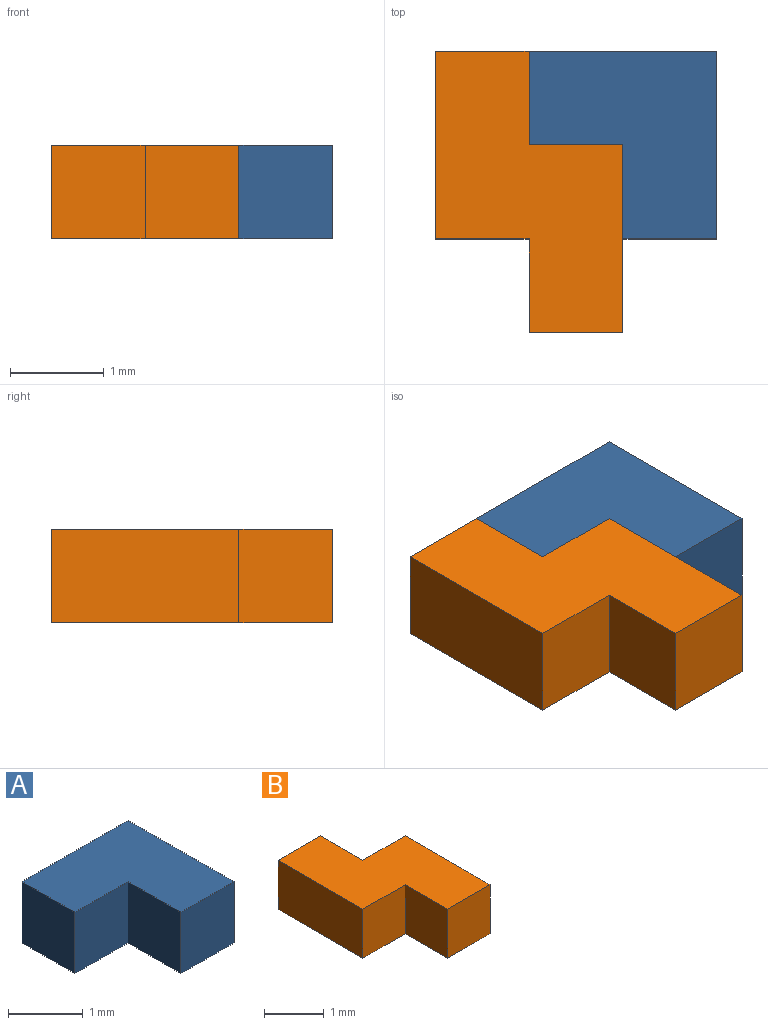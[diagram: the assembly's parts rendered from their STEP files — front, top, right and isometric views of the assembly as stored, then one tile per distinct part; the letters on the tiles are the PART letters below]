
ASSEMBLY  parts=2 mates=1
PART A: 8 faces, bbox 2x2x1 mm
  f0: plane 1x1mm, normal (-1,0,0), area 1mm2, adj f1,f3,f4,f5
  f1: plane 2x2mm, normal (0,0,-1), area 3mm2, adj f0,f2,f4,f5,f6,f7
  f2: plane 2x1mm, normal (1,0,0), area 2mm2, adj f1,f3,f5,f7
  f3: plane 2x2mm, normal (0,0,1), area 3mm2, adj f0,f2,f4,f5,f6,f7
  f4: plane 1x1mm, normal (0,-1,0), area 1mm2, adj f0,f1,f3,f6
  f5: plane 2x1mm, normal (0,1,0), area 2mm2, adj f0,f1,f2,f3
  f6: plane 1x1mm, normal (-1,0,0), area 1mm2, adj f1,f3,f4,f7
  f7: plane 1x1mm, normal (0,-1,0), area 1mm2, adj f1,f2,f3,f6
PART B: 10 faces, bbox 2x3x1 mm
  f0: plane 3x2mm, normal (0,0,-1), area 4mm2, adj f1,f3,f4,f5,f6,f7,f8,f9
  f1: plane 1x1mm, normal (1,0,0), area 1mm2, adj f0,f2,f5,f6
  f2: plane 3x2mm, normal (0,0,1), area 4mm2, adj f1,f3,f4,f5,f6,f7,f8,f9
  f3: plane 2x1mm, normal (-1,0,0), area 2mm2, adj f0,f2,f4,f5
  f4: plane 1x1mm, normal (0,-1,0), area 1mm2, adj f0,f2,f3,f8
  f5: plane 1x1mm, normal (0,1,0), area 1mm2, adj f0,f1,f2,f3
  f6: plane 1x1mm, normal (0,1,0), area 1mm2, adj f0,f1,f2,f7
  f7: plane 2x1mm, normal (1,0,0), area 2mm2, adj f0,f2,f6,f9
  f8: plane 1x1mm, normal (-1,0,0), area 1mm2, adj f0,f2,f4,f9
  f9: plane 1x1mm, normal (0,-1,0), area 1mm2, adj f0,f2,f7,f8
PLACE A t=(-1.58,0.53,-0.59)mm
PLACE B t=(-1.58,0.53,-0.59)mm
MATE fastened A.f4 <-> B.f6  axis (0,-1,0) through (-1.08,-0.47,-0.09)mm
